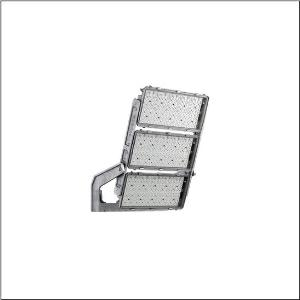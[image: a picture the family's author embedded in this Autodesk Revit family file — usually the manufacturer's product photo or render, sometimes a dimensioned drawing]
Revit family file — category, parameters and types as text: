
# Revit family: floodlight_fl_11_maxi_pro_remote___pl43_5xa779524a01ba_c92a
name_source: partatom
category: Lighting Fixtures
units: mm (PartAtom-declared; Revit-internal decimal feet)

## family parameters
Cut with Voids When Loaded = No
Host = Face
Light Source = No
Part Type = Normal
Room Calculation Point = No
Round Connector Dimension = Use Diameter
Shared = No

## types (1)
- --- (1 x LED, 108940 lm, 1020.5 W, 5700K)
    Apparent Load = 1020 VA
    CIE Flux Codes = 25 74 99 100 100
    Color Rendering = 90
    Color Temperature = 5700K
    Default Elevation = 1800 mm
    Description = Floodlight FL 11  maxi  pro Remote floodlight; light control with lens of PMMA; cover panel of toughened safety glass, transparent; light distribution: PL43, asymmetric direct distribution, LEDcolour temperature: 5700K, rated luminous flux: 108.940lm, colour rendering: CRI > 90, light colour: 957; luminous efficacy: 107lm/W; brightness control: DMX+RDM; with terminal, 8-pole, max. 2.5mm², mains connection: 220..240V/380..400V AC, 50/60Hz, surge voltage resistance: line to ground: 10kV, ECG replaceable separately, LED unit replaceable without ESD environment, dustproof LED module, dimming range 10..100%; 1021W floodlight with 3x LED unit of diecast aluminium, coated grey; length: 713mm / width: 651mm / height: 338mm; mounting bracket, of diecast aluminium, uncoated, natural, equipment: Longlife, protection rating (complete): IP66; insulation class (complete): insulation class I (protective earthing); certification: CE, ENEC, VDE; ball protection: ball impact resistance with accessories, impact resistance: IK07; only for outdoor installations, rated ambient temperature 10°C, permissible operating ambient temperature: -40..+40°C, permissible storage temperature: -40..+85°C; packaging unit: 1 piece

Light Distribution: PL43
    Height = 320 mm
    Lamp = 1 x LED
    Lamp Light Flux = 108940 lm
    Lamp Power = 1020.5 W
    Lamp count = 1
    Length = 1002 mm
    Luminous efficacy = 107 lm/W
    Manufacturer = Siteco
    ModVariant = No
    Model = 5XA779524A01BA
    Mounting Place = Ceiling
    Mounting Type = Surface mounted
    Number of Poles = 1
    OnlyDefault = Yes
    Power Factor = 1
    Product Name = Floodlight FL 11 maxi pro Remote | PL43
    Product group = floodlight | ceiling mounted
    ProductGroupID = 302
    Protection Class = Protection class I
    Protection Degree = IP 66
    RLX_Detail_Level = 1
    RLX_Emergency_Light_Flux = 0 lm
    RLX_Emergency_Type = 0
    RLX_Emergency_Type_DB = No
    RlxData = <blob elided: 52209 chars, md5=c403ea5d>
    Socket = socket
    Standby Power = 0 W
    System Light Flux = 108940 lm
    System Power = 1020 W
    Type Comments = factory setting: luminous flux: 100 % | dim-lin: 255 | 710 mA
    Type Image = l_1006784.jpg
    URL = http://relux.com
    VarID = @adj_027015
    Voltage = 0 V
    Weight = 0.00 kg
    Width = 655 mm

## geometry (parser evidence)
native form markers: Blend x4, Sweep x13
no freeform markers — native parametric forms only
